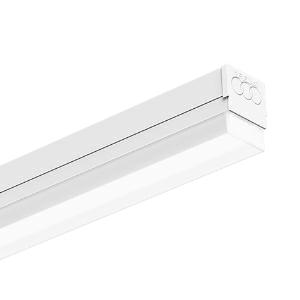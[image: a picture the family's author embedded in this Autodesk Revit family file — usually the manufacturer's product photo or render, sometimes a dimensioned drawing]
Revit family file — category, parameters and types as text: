
# Revit family: 3f_filippi_-_3f_zeta_dr_as_3f_filippi_-_10887_-_3f_zeta_dr_as_2x22_led_l1489
name_source: partatom
category: Lighting Fixtures
units: mm (PartAtom-declared; Revit-internal decimal feet)

## family parameters
Cut with Voids When Loaded = No
Host = Face
Light Source = No
Part Type = Normal
Room Calculation Point = No
Round Connector Dimension = Use Diameter
Shared = No

## types (1)
- 3F Filippi - 3F Zeta DR AS (1 x LED, 5096 lm, 49 W, 4000 K)
    Apparent Load = 49 VA
    Approval mark = CE
    CIE Flux Codes = 43 73 92 90 100
    Color Rendering = 80
    Color Temperature = 4000 K
    Control Gear = Electronic ballast
    Default Elevation = 1800 mm
    Description = ILLUMINOTECHNICAL
Luminous efficiency 100% (DLOR 90%, ULOR 10%).
Initial luminous flux of the luminaire 5096 lm.
Diffused asymmetric distribution.
Installation Interdistance Transv.D = 1.31 x hu - Long.D = 1.25 x hu.
Beam angle: 122° - 111°.
Luminous efficacy 104 lm/W.
Lifetime (L93/B10): 30000 h. (tq+25°C)
Lifetime (L90/B10): 50000 h. (tq+25°C)
Lifetime (L85/B10): 80000 h. (tq+25°C)
Lifetime (L80/B10): 100000 h. (tq+25°C)
Sudden decreased luminous flux after 50000 hours: 0% (C0).
Photobiological safety in compliance with IEC/TR 62778: RG0 risk exempt, (IEC 62471).
In compliance with IEC/EN 62722-2-1 - IEC/EN 62717 standards.

SOURCE
2 linear LED modules 22W/840.
Energy efficiency class (UE 2019/2020 - UE 2019/2015): D.
CIE 13.3 Colour rendering index: CRI >80 (R9 <50%).
IES TM-30 Fidelity Index: Rf = 84 Rg = 95.
CCT nominal colour temperature 4000 K.
Colour initial tolerance (MacAdam): SDCM 3.

MECHANICAL
Housing in hot-galvanised steel, painted in white polyester, obtained through rolling process.
Light unit in hot-galvanised steel, painted in white polyester base with fixing springs and retractable safety hooks in stainless steel.
Rectangular screen in self-extinguishing polycarbonate, UV stabilised, opal, with smooth outer surface.
End caps in white polycarbonate.
Pair of stainless steel sliding brackets with sliding block screws.
Luminaire with limited surface temperature. - D - (EN 60598-2-24)
Dimensions: 1489x62 mm, height 81 mm. Weight 4.04 kg.
IP40 protection degree.
Mechanical strength to impacts IK06 (1 joule).
Glow-wire test resistance 850°C.

ELECTRICAL
Halogen Free electronic wiring 230V-50/60Hz, power factor 0.95, THD <25%, constant output current, SELV, class I, 1 driver.
Power of the luminaire 49 W.
ENEC - CE.
SAFE FLICKER: PstLM=<1 and SVM=<0.4 (IEC TR 61547-1 and IEC TR 63158), to ensure a more comfortable and safe light.
Luminaire compliant with EN 60598-2-22 for power supply from a centralised emergency system CPSS (Central Power Supply System), not incorporated in the luminaire - high risk areas excluded. The default power and flux are 100% in AC and 100% in DC.
Ambient temperature from 0°C to +25°C.
Temperature class T6 max 85°C.
Relative humidity UR: <85%.

INSTALLATION
Ceiling / Suspended / Wall.
All accessories dedicated to this product are available on the Catalog and on our website www.3F-Filippi.com.

APPLICATIONS
Suitable product for food production plants (HACCP), IFS (Food Version 6), BRC (GSFS Food Version 7).
In commercial environments, exhibition areas, shops and stores.

WARNING
Luminaire designed for disposal/recycling at end-of-life.
Replaceable (LED only) light source by a professional. Replaceable control gear by a professional.
    Height = 81 mm
    Lamp = 1 x LED
    Lamp Light Flux = 5096 lm
    Lamp Power = 49 W
    Lamp count = 1
    Length = 1489 mm
    Lifetime = 50000 h
    Luminous efficacy = 104 lm/W
    Manufacturer = 3F Filippi
    ModVariant = No
    Model = 3F Filippi - 10887 - 3F Zeta DR AS 2x22 LED L1489
    Mounting Place = Ceiling
    Mounting Type = Pendant
    Number of Poles = 1
    OnlyDefault = Yes
    Power Factor = 1
    Product Name = 3F Filippi - 3F Zeta DR AS
    Product group = pendant luminaire
    ProductGroupID = 9
    Protection Class = Protection class I
    Protection Degree = IP 40
    RLX_Detail_Level = 1
    RLX_Emergency_Light_Flux = 0 lm
    RLX_Emergency_Type = 0
    RLX_Emergency_Type_DB = No
    RlxData = <blob elided: 57133 chars, md5=1c20bf89>
    Socket = socket
    Standby Power = 0 W
    System Light Flux = 5096 lm
    System Power = 49 W
    Type Comments = Product without accessories
    Type Image = 3ffilippi_3f_zeta_dr_as.jpg
    URL = http://relux.com
    VarID = ---
    Voltage = 0 V
    Weight = 0.00 kg
    Width = 62 mm  [stored 0.203412 ft]

note: [stored X ft] marks values corroborated as IEEE doubles in the binary element streams (Revit-internal decimal feet)

## geometry (parser evidence)
native form markers: Blend x4, Sweep x15
no freeform markers — native parametric forms only
